annotation { "Feature Type Name" : "Feature", "Feature Type Description" : "" }
export const myFeature = defineFeature(function(context is Context, id is Id, definition is map)
    precondition{}
    {
        {
            var Q0;
            Q0=qCreatedBy(makeId("Front.planeOp"),FACE);
            var sketch = newSketch(context, id + "F0", { "sketchPlane" : qUnion([Q0])});
            skFitSpline(sketch, "E0", {"points": [v(0, -73.31) * mm, v(-24.48, -71.7) * mm, v(-36.71, -66.39) * mm, v(-42.49, -59.23) * mm, v(-46.18, -49.3) * mm, v(-46.87, -37.3) * mm, v(-42.95, -24.36) * mm, v(-36.72, -17.13) * mm, v(-28.97, -12.23) * mm, v(-24.69, -10.67) * mm, v(-24.88, -9.9) * mm, v(-29.61, -9.12) * mm, v(-29.55, -7.5) * mm, v(-21.64, -4.88) * mm, v(-3.2, -6.22) * mm, v(0, -5.51) * mm, v(0, -5.51) * mm], "startDerivative": vector(-191.51, -13.65) * mm, "endDerivative": vector(0.02, -107.95) * mm});
            skLineSegment(sketch, "E1", {"start": v(0, -5.51) * mm, "end": v(0, -5.51) * mm});
            skLineSegment(sketch, "E2", {"start": v(-29.61, -9.12) * mm, "end": v(-29.55, -7.5) * mm});
            skLineSegment(sketch, "E3", {"start": v(-29.55, -7.5) * mm, "end": v(0, -7.5) * mm});
            skLineSegment(sketch, "E4.trimOffspring", {"start": v(0, -7.5) * mm, "end": v(0, -73.31) * mm});
            skSolve(sketch);
        }
        {
            var Q0;
            Q0=makeQuery(id+"F0.imprint","IMPRINT",FACE,{"disambiguationData":[TD([[makeQuery(id+"F0.imprint","IMPRINT",EDGE,{"derivedFrom":sQuery(id+"F0.wireOp",EDGE,"E0")}),-1.0]])]});
            var Q1;
            Q1=sQuery(id+"F0.wireOp",EDGE,"E4.trimOffspring");
            revolve(context, id + "F1", {"entities" : qUnion([Q0]), "axis" : qUnion([Q1]), "revolveType" : RevolveType.FULL});
        }
        {
            var Q0;
            Q0=qCreatedBy(makeId("Front.planeOp"),FACE);
            var sketch = newSketch(context, id + "F2", { "sketchPlane" : qUnion([Q0])});
            skText(sketch, "E5", { "text": "TOIL TROUBLE   ", "fontName": "NotoSansCJKtc-Regular.otf"});
            const initialGuessF2  = {"E5": [-0.03617, -0.0303, 1, 0, 0.00783], "E5": [-0.03617, -0.0303, 1, 0, 0.00783]};
            skSetInitialGuess(sketch, initialGuessF2);
            skSolve(sketch);
        }
        {
            var Q0;
            Q0 = qSketchRegion(id + "F2", true);
            extrude(context, id + "F3", {"entities" : qUnion([Q0]), "operationType" : NewBodyOperationType.REMOVE, "depth" : 46.04 * mm});
        }
        {
            var Q0;
            Q0=qCreatedBy(makeId("Top.planeOp"),FACE);
            var sketch = newSketch(context, id + "F4", { "sketchPlane" : qUnion([Q0])});
            skCircle(sketch, "E6", {"center": v(0, 0) * mm, "radius": 23.34 * mm});
            skSolve(sketch);
        }
        {
            var Q0;
            Q0=makeQuery(id+"F4.imprint","IMPRINT",FACE,{"disambiguationData":[TD([[makeQuery(id+"F4.imprint","IMPRINT",EDGE,{"derivedFrom":sQuery(id+"F4.wireOp",EDGE,"E6")}),1.0]])]});
            extrude(context, id + "F5", {"entities" : qUnion([Q0]), "operationType" : NewBodyOperationType.REMOVE, "oppositeDirection" : true, "depth" : 12.7 * mm});
        }
        {
            var Q0;
            Q0=qCreatedBy(makeId("Front.planeOp"),FACE);
            var sketch = newSketch(context, id + "F6", { "sketchPlane" : qUnion([Q0])});
            skText(sketch, "E7", { "text": "TOIL TROUBLE", "fontName": "NotoSansCJKtc-Regular.otf"});
            const initialGuessF6  = {"E7": [-0.0392, -0.0567, 1, 0, 0.0083]};
            skSetInitialGuess(sketch, initialGuessF6);
            skSolve(sketch);
        }
        {
            var Q0;
            Q0 = qSketchRegion(id + "F6", true);
            extrude(context, id + "F7", {"entities" : qUnion([Q0]), "operationType" : NewBodyOperationType.REMOVE, "depth" : 50.8 * mm});
        }
        {
            var Q0;
            Q0=qCreatedBy(makeId("Front.planeOp"),FACE);
            var sketch = newSketch(context, id + "F8", { "sketchPlane" : qUnion([Q0])});
            skEllipse(sketch, "E8", {"center": v(-25.64, -26.39) * mm, "majorRadius": 3.58 * mm, "minorRadius": 3.05 * mm, "majorAxis": v(0, 1)});
            skEllipse(sketch, "E9", {"center": v(7.31, -26.41) * mm, "majorRadius": 3.52 * mm, "minorRadius": 2.8 * mm, "majorAxis": v(0, 1)});
            skLineSegment(sketch, "E10", {"start": v(-1.74, -22.74) * mm, "end": v(-1.74, -26.6) * mm});
            skLineSegment(sketch, "E11", {"start": v(-1.74, -26.6) * mm, "end": v(0.71, -26.5) * mm});
            skLineSegment(sketch, "E12", {"start": v(0.71, -26.5) * mm, "end": v(1.98, -25.27) * mm});
            skLineSegment(sketch, "E13", {"start": v(1.98, -25.27) * mm, "end": v(2.1, -23.92) * mm});
            skLineSegment(sketch, "E14", {"start": v(2.1, -23.92) * mm, "end": v(1.36, -22.95) * mm});
            skLineSegment(sketch, "E15", {"start": v(1.36, -22.95) * mm, "end": v(-1.74, -22.74) * mm});
            skLineSegment(sketch, "E16", {"start": v(21.13, -22.92) * mm, "end": v(21.13, -29.8) * mm});
            skLineSegment(sketch, "E17", {"start": v(21.13, -29.8) * mm, "end": v(23.73, -29.9) * mm});
            skLineSegment(sketch, "E18", {"start": v(23.73, -29.9) * mm, "end": v(25.36, -28.6) * mm});
            skLineSegment(sketch, "E19", {"start": v(25.36, -28.6) * mm, "end": v(25.27, -27.52) * mm});
            skLineSegment(sketch, "E20", {"start": v(25.27, -27.52) * mm, "end": v(24.4, -26.43) * mm});
            skLineSegment(sketch, "E21", {"start": v(24.4, -26.43) * mm, "end": v(23.77, -26.3) * mm});
            skLineSegment(sketch, "E22", {"start": v(23.77, -26.3) * mm, "end": v(24.23, -25.57) * mm});
            skLineSegment(sketch, "E23", {"start": v(24.23, -25.57) * mm, "end": v(24.88, -24.78) * mm});
            skLineSegment(sketch, "E24", {"start": v(24.88, -24.78) * mm, "end": v(24.88, -23.52) * mm});
            skLineSegment(sketch, "E25", {"start": v(24.88, -23.52) * mm, "end": v(23.72, -22.88) * mm});
            skLineSegment(sketch, "E26", {"start": v(23.72, -22.88) * mm, "end": v(21.13, -22.92) * mm});
            skEllipse(sketch, "E27", {"center": v(-27.96, -52.78) * mm, "majorRadius": 3.93 * mm, "minorRadius": 3.05 * mm, "majorAxis": v(0, 1)});
            skLineSegment(sketch, "E28", {"start": v(-2.84, -48.75) * mm, "end": v(-2.84, -52.6) * mm});
            skLineSegment(sketch, "E29", {"start": v(-2.84, -52.6) * mm, "end": v(-0.97, -52.73) * mm});
            skLineSegment(sketch, "E30", {"start": v(-0.97, -52.73) * mm, "end": v(0, -52.48) * mm});
            skLineSegment(sketch, "E31", {"start": v(0, -52.48) * mm, "end": v(1.02, -52.1) * mm});
            skLineSegment(sketch, "E32", {"start": v(1.02, -52.1) * mm, "end": v(1.34, -49.58) * mm});
            skLineSegment(sketch, "E33", {"start": v(1.34, -49.58) * mm, "end": v(0.97, -49.17) * mm});
            skLineSegment(sketch, "E34", {"start": v(0.97, -49.17) * mm, "end": v(0, -48.85) * mm});
            skLineSegment(sketch, "E35", {"start": v(0, -48.85) * mm, "end": v(-1.65, -48.85) * mm});
            skLineSegment(sketch, "E36", {"start": v(-1.65, -48.85) * mm, "end": v(-2.84, -48.75) * mm});
            skEllipse(sketch, "E37", {"center": v(6.96, -52.63) * mm, "majorRadius": 3.84 * mm, "minorRadius": 2.82 * mm, "majorAxis": v(0, 1)});
            skLineSegment(sketch, "E38", {"start": v(21.63, -49.07) * mm, "end": v(21.63, -56.24) * mm});
            skLineSegment(sketch, "E39", {"start": v(21.63, -56.24) * mm, "end": v(23.73, -56.24) * mm});
            skLineSegment(sketch, "E40", {"start": v(23.73, -56.24) * mm, "end": v(24.86, -56.03) * mm});
            skLineSegment(sketch, "E41", {"start": v(24.86, -56.03) * mm, "end": v(25.82, -55.3) * mm});
            skLineSegment(sketch, "E42", {"start": v(25.82, -55.3) * mm, "end": v(26.2, -54.5) * mm});
            skLineSegment(sketch, "E43", {"start": v(26.2, -54.5) * mm, "end": v(25.99, -53.4) * mm});
            skLineSegment(sketch, "E44", {"start": v(25.99, -53.4) * mm, "end": v(25.36, -52.9) * mm});
            skLineSegment(sketch, "E45", {"start": v(25.36, -52.9) * mm, "end": v(24.6, -52.55) * mm});
            skLineSegment(sketch, "E46", {"start": v(24.6, -52.55) * mm, "end": v(24.4, -52) * mm});
            skLineSegment(sketch, "E47", {"start": v(24.4, -52) * mm, "end": v(24.79, -51.81) * mm});
            skLineSegment(sketch, "E48", {"start": v(24.79, -51.81) * mm, "end": v(25.66, -50.04) * mm});
            skLineSegment(sketch, "E49", {"start": v(25.66, -50.04) * mm, "end": v(25.1, -49.28) * mm});
            skLineSegment(sketch, "E50", {"start": v(25.1, -49.28) * mm, "end": v(23.8, -48.7) * mm});
            skLineSegment(sketch, "E51", {"start": v(23.8, -48.7) * mm, "end": v(22.05, -48.68) * mm});
            skLineSegment(sketch, "E52", {"start": v(22.05, -48.68) * mm, "end": v(21.63, -49.07) * mm});
            skSolve(sketch);
        }
        {
            var Q0;
            Q0=makeQuery(id+"F8.imprint","IMPRINT",FACE,{"disambiguationData":[TD([[makeQuery(id+"F8.imprint","IMPRINT",EDGE,{"derivedFrom":sQuery(id+"F8.wireOp",EDGE,"E8")}),1.0]])]});
            var Q1;
            Q1=makeQuery(id+"F8.imprint","IMPRINT",FACE,{"disambiguationData":[TD([[makeQuery(id+"F8.imprint","IMPRINT",EDGE,{"derivedFrom":sQuery(id+"F8.wireOp",EDGE,"E9")}),1.0]])]});
            var Q2;
            Q2=makeQuery(id+"F8.imprint","IMPRINT",FACE,{"disambiguationData":[TD([[makeQuery(id+"F8.imprint","IMPRINT",EDGE,{"derivedFrom":sQuery(id+"F8.wireOp",EDGE,"E16")}),1.0]])]});
            var Q3;
            Q3=makeQuery(id+"F8.imprint","IMPRINT",FACE,{"disambiguationData":[TD([[makeQuery(id+"F8.imprint","IMPRINT",EDGE,{"derivedFrom":sQuery(id+"F8.wireOp",EDGE,"E10")}),1.0]])]});
            var Q4;
            Q4=makeQuery(id+"F8.imprint","IMPRINT",FACE,{"disambiguationData":[TD([[makeQuery(id+"F8.imprint","IMPRINT",EDGE,{"derivedFrom":sQuery(id+"F8.wireOp",EDGE,"E38")}),1.0]])]});
            var Q5;
            Q5=makeQuery(id+"F8.imprint","IMPRINT",FACE,{"disambiguationData":[TD([[makeQuery(id+"F8.imprint","IMPRINT",EDGE,{"derivedFrom":sQuery(id+"F8.wireOp",EDGE,"E37")}),1.0]])]});
            var Q6;
            Q6=makeQuery(id+"F8.imprint","IMPRINT",FACE,{"disambiguationData":[TD([[makeQuery(id+"F8.imprint","IMPRINT",EDGE,{"derivedFrom":sQuery(id+"F8.wireOp",EDGE,"E28")}),1.0]])]});
            var Q7;
            Q7=makeQuery(id+"F8.imprint","IMPRINT",FACE,{"disambiguationData":[TD([[makeQuery(id+"F8.imprint","IMPRINT",EDGE,{"derivedFrom":sQuery(id+"F8.wireOp",EDGE,"E27")}),1.0]])]});
            extrude(context, id + "F9", {"entities" : qUnion([Q0, Q1, Q2, Q3, Q4, Q5, Q6, Q7]), "operationType" : NewBodyOperationType.REMOVE, "depth" : 53.86 * mm});
        }
    });